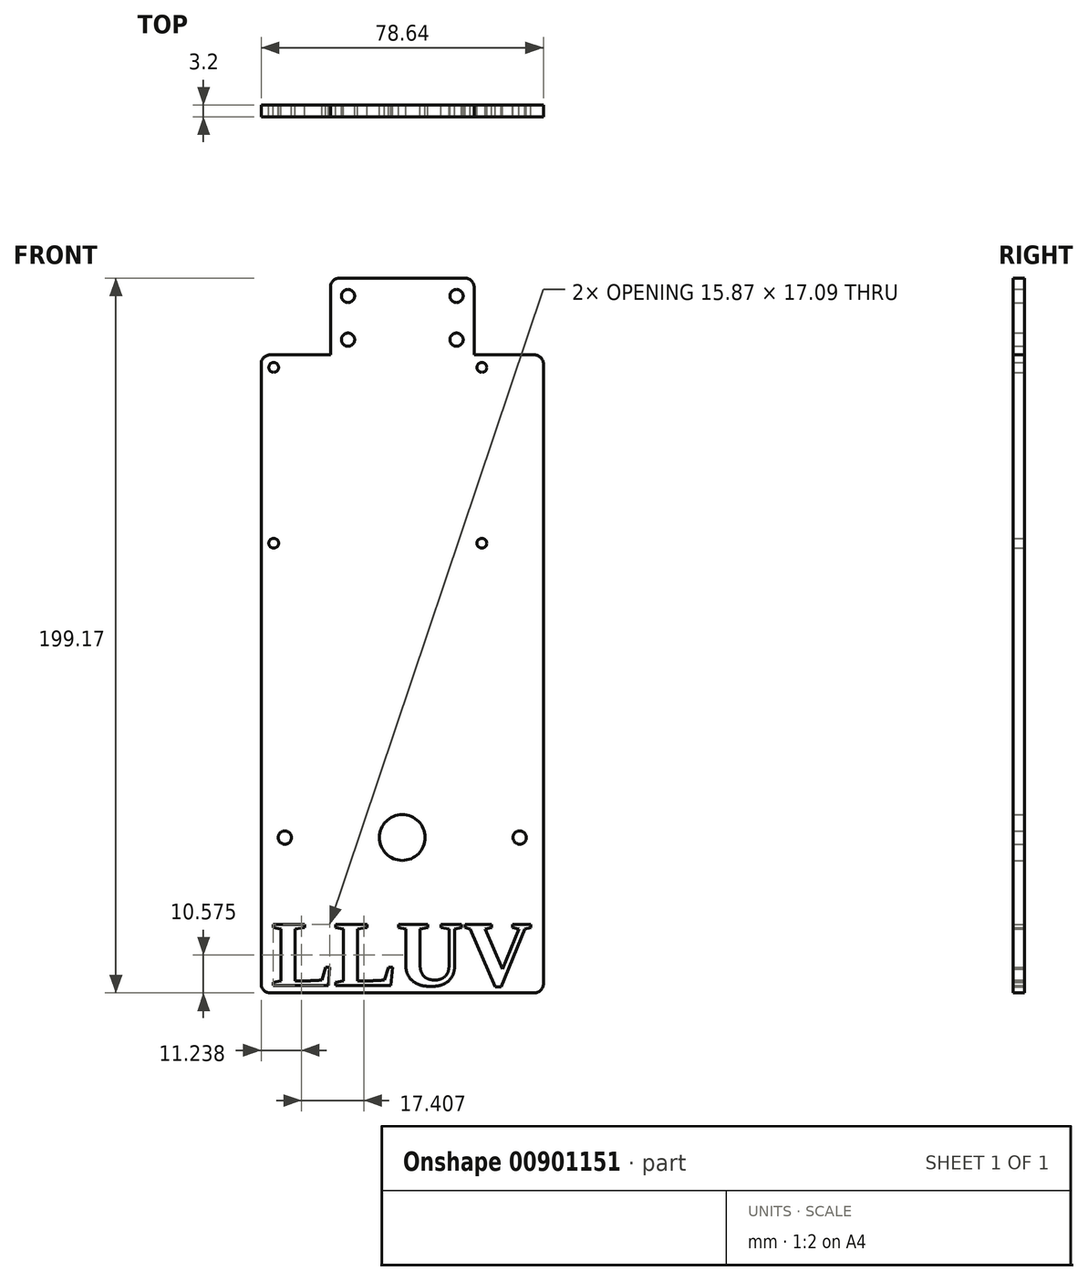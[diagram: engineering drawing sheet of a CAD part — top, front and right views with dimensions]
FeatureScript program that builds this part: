
annotation { "Feature Type Name" : "Feature", "Feature Type Description" : "" }
export const myFeature = defineFeature(function(context is Context, id is Id, definition is map)
    precondition{}
    {
        {
            var Q0;
            Q0=qCreatedBy(makeId("Front.planeOp"),FACE);
            var sketch = newSketch(context, id + "F0", { "sketchPlane" : qUnion([Q0])});
            skLineSegment(sketch, "E0.bottom", {"start": v(-79.69, -96.86) * mm, "end": v(-1.05, -96.86) * mm, "construction": true});
            skLineSegment(sketch, "E0.top", {"start": v(-77.15, -274.66) * mm, "end": v(-3.59, -274.66) * mm});
            skLineSegment(sketch, "E0.left", {"start": v(-79.69, -99.4) * mm, "end": v(-79.69, -272.12) * mm});
            skLineSegment(sketch, "E0.right", {"start": v(-1.05, -99.4) * mm, "end": v(-1.05, -272.12) * mm});
            skLineSegment(sketch, "E1", {"start": v(-60.38, -96.86) * mm, "end": v(-60.38, -78.03) * mm});
            skLineSegment(sketch, "E2", {"start": v(-57.84, -75.5) * mm, "end": v(-22.9, -75.5) * mm});
            skLineSegment(sketch, "E3", {"start": v(-20.35, -78.03) * mm, "end": v(-20.35, -96.86) * mm});
            skCircle(sketch, "E4", {"center": v(-73.08, -231.38) * mm, "radius": 1.85 * mm});
            skCircle(sketch, "E5", {"center": v(-7.66, -231.38) * mm, "radius": 1.85 * mm});
            skCircle(sketch, "E6", {"center": v(-55.48, -80.46) * mm, "radius": 1.85 * mm});
            skCircle(sketch, "E7", {"center": v(-25.26, -80.46) * mm, "radius": 1.85 * mm});
            skLineSegment(sketch, "E8", {"start": v(-77.15, -96.86) * mm, "end": v(-60.38, -96.86) * mm});
            skLineSegment(sketch, "E9", {"start": v(-20.35, -96.86) * mm, "end": v(-3.59, -96.86) * mm});
            skCircle(sketch, "E10", {"center": v(-76.18, -100.37) * mm, "radius": 1.37 * mm});
            skCircle(sketch, "E11", {"center": v(-18.2, -100.37) * mm, "radius": 1.37 * mm});
            skCircle(sketch, "E12", {"center": v(-76.18, -149.36) * mm, "radius": 1.37 * mm});
            skCircle(sketch, "E13", {"center": v(-18.2, -149.36) * mm, "radius": 1.37 * mm});
            skCircle(sketch, "E14", {"center": v(-55.48, -92.63) * mm, "radius": 1.85 * mm});
            skCircle(sketch, "E15", {"center": v(-25.26, -92.63) * mm, "radius": 1.85 * mm});
            skCircle(sketch, "E16", {"center": v(-40.36, -231.38) * mm, "radius": 6.38 * mm});
            skText(sketch, "E17", { "text": "LLUV", "fontName": "Tinos-Bold.ttf"});
            skPoint(sketch, "E18.visualSharp", {"position": v(-79.69, -96.86) * mm});
            skArc(sketch, "E18.filletArc", {"start": v(-77.15, -96.86) * mm, "mid": v(-78.95, -97.6) * mm, "end": v(-79.69, -99.4) * mm});
            skPoint(sketch, "E19.visualSharp", {"position": v(-1.05, -96.86) * mm});
            skArc(sketch, "E19.filletArc", {"start": v(-1.05, -99.4) * mm, "mid": v(-1.8, -97.6) * mm, "end": v(-3.59, -96.86) * mm});
            skPoint(sketch, "E20.visualSharp", {"position": v(-1.05, -274.66) * mm});
            skArc(sketch, "E20.filletArc", {"start": v(-3.59, -274.66) * mm, "mid": v(-1.8, -273.92) * mm, "end": v(-1.05, -272.12) * mm});
            skPoint(sketch, "E21.visualSharp", {"position": v(-79.69, -274.66) * mm});
            skArc(sketch, "E21.filletArc", {"start": v(-79.69, -272.12) * mm, "mid": v(-78.95, -273.92) * mm, "end": v(-77.15, -274.66) * mm});
            skPoint(sketch, "E22.visualSharp", {"position": v(-60.38, -75.5) * mm});
            skArc(sketch, "E22.filletArc", {"start": v(-57.84, -75.5) * mm, "mid": v(-59.64, -76.24) * mm, "end": v(-60.38, -78.03) * mm});
            skPoint(sketch, "E23.visualSharp", {"position": v(-20.35, -75.5) * mm});
            skArc(sketch, "E23.filletArc", {"start": v(-20.35, -78.03) * mm, "mid": v(-21.1, -76.24) * mm, "end": v(-22.9, -75.5) * mm});
            const initialGuessF0  = {"E17": [-0.07683, -0.27263, 1, 0, 0.01879]};
            skSetInitialGuess(sketch, initialGuessF0);
            skSolve(sketch);
        }
        {
            var Q0;
            Q0 = qSketchRegion(id + "F0", true);
            extrude(context, id + "F1", {"entities" : qUnion([Q0]), "depth" : 3.2 * mm, "offsetDistance" : 25.4 * mm});
        }
    });
